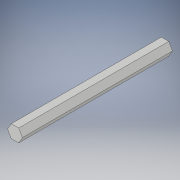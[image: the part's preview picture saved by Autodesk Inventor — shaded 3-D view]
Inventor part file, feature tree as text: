
AUTODESK INVENTOR PART (.ipt)
format: ipt  version: 2018 (Build 220112000, 112)  size: 95,232 bytes
history: native  units: in
note: dims shown in document units (in); Inventor stores cm internally (conversion verified against a paired STEP export)
features: extrude x1, sketch x1
ambient origin geometry x8: Origin, YZ Plane, XZ Plane, XY Plane, X Axis, Y Axis, Z Axis, Center Point
bodies: Solid1 (feature_tree)
feature tree (2):
  extrude  "Extrusion1"  Depth=3.5in TaperAngle=0.0deg
  sketch  "Sketch1"  dims[d0=0.3in d1=3.5in d2=0.0in]
